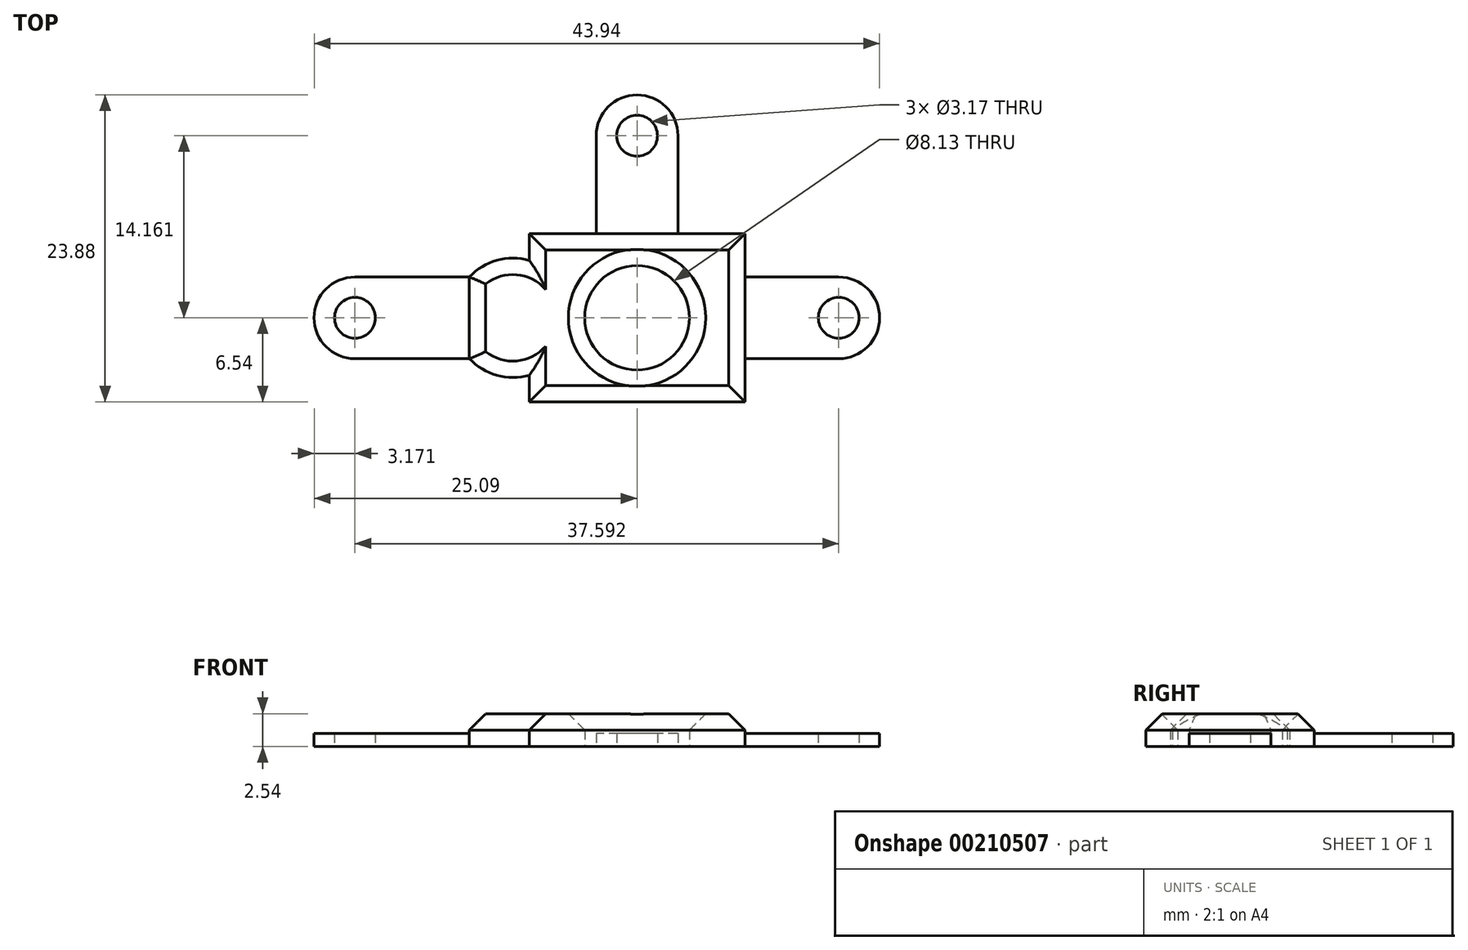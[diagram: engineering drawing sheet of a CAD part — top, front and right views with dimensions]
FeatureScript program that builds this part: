
annotation { "Feature Type Name" : "Feature", "Feature Type Description" : "" }
export const myFeature = defineFeature(function(context is Context, id is Id, definition is map)
    precondition{}
    {
        {
            var Q0;
            Q0=qCreatedBy(makeId("Top.planeOp"),FACE);
            var sketch = newSketch(context, id + "F0", { "sketchPlane" : qUnion([Q0])});
            skPoint(sketch, "E0.middle", {"position": v(0, 0) * mm});
            skArc(sketch, "E1", {"start": v(-8.38, 4.46) * mm, "mid": v(-10.89, 4.47) * mm, "end": v(-13.03, 3.17) * mm});
            skPoint(sketch, "E1.centerSnap0", {"position": v(-6.78, 0) * mm});
            skCircle(sketch, "E2", {"center": v(0, 0) * mm, "radius": 4.06 * mm});
            skArc(sketch, "E3", {"start": v(3.17, 14.16) * mm, "mid": v(0, 17.34) * mm, "end": v(-3.18, 14.16) * mm});
            skLineSegment(sketch, "E4", {"start": v(6.78, 0) * mm, "end": v(-13.03, 0) * mm, "construction": true});
            skLineSegment(sketch, "E5", {"start": v(3.17, 14.16) * mm, "end": v(3.18, 6.54) * mm});
            skLineSegment(sketch, "E6", {"start": v(-3.18, 14.16) * mm, "end": v(-3.18, 6.54) * mm});
            skArc(sketch, "E7.MirrorCS", {"start": v(3.17, -14.16) * mm, "mid": v(0, -17.34) * mm, "end": v(-3.18, -14.16) * mm});
            skLineSegment(sketch, "E8.MirrorCS", {"start": v(3.18, -14.16) * mm, "end": v(3.18, -6.54) * mm});
            skLineSegment(sketch, "E9.MirrorCS", {"start": v(-3.17, -14.16) * mm, "end": v(-3.17, -6.54) * mm});
            skArc(sketch, "E10", {"start": v(-21.92, 3.18) * mm, "mid": v(-25.1, 0) * mm, "end": v(-21.92, -3.18) * mm});
            skLineSegment(sketch, "E11", {"start": v(-21.92, 3.18) * mm, "end": v(-13.03, 3.18) * mm});
            skLineSegment(sketch, "E12", {"start": v(-21.92, -3.18) * mm, "end": v(-13.03, -3.18) * mm});
            skArc(sketch, "E13.trimOffspring", {"start": v(-13.03, -3.18) * mm, "mid": v(-10.89, -4.47) * mm, "end": v(-8.38, -4.46) * mm});
            skArc(sketch, "E14", {"start": v(15.67, -3.17) * mm, "mid": v(18.85, 0) * mm, "end": v(15.67, 3.18) * mm});
            skLineSegment(sketch, "E15", {"start": v(15.67, 3.18) * mm, "end": v(8.38, 3.17) * mm});
            skLineSegment(sketch, "E16", {"start": v(15.67, -3.17) * mm, "end": v(8.38, -3.17) * mm});
            skCircle(sketch, "E17", {"center": v(0, 14.16) * mm, "radius": 1.59 * mm});
            skCircle(sketch, "E18", {"center": v(15.67, 0) * mm, "radius": 1.59 * mm});
            skCircle(sketch, "E19", {"center": v(-21.92, 0) * mm, "radius": 1.59 * mm});
            skCircle(sketch, "E20", {"center": v(0, -14.16) * mm, "radius": 1.59 * mm});
            skLineSegment(sketch, "E21", {"start": v(-13.03, 3.18) * mm, "end": v(-13.03, -3.18) * mm});
            skLineSegment(sketch, "E22.bottom", {"start": v(8.38, 6.54) * mm, "end": v(-8.38, 6.54) * mm});
            skLineSegment(sketch, "E22.top", {"start": v(8.38, -6.54) * mm, "end": v(-8.38, -6.54) * mm});
            skLineSegment(sketch, "E22.left", {"start": v(8.38, 6.54) * mm, "end": v(8.38, -6.54) * mm});
            skLineSegment(sketch, "E22.right", {"start": v(-8.38, 6.54) * mm, "end": v(-8.38, -6.54) * mm});
            skSolve(sketch);
        }
        {
            var Q0;
            Q0=makeQuery(id+"F0.imprint","IMPRINT",FACE,{"disambiguationData":[TD([[makeQuery(id+"F0.imprint","IMPRINT",EDGE,{"derivedFrom":sQuery(id+"F0.wireOp",EDGE,"E0.bottom")}),1.0]])]});
            var Q1;
            Q1=makeQuery(id+"F0.imprint","IMPRINT",FACE,{"disambiguationData":[TD([[makeQuery(id+"F0.imprint","IMPRINT",EDGE,{"derivedFrom":sQuery(id+"F0.wireOp",EDGE,"E2")}),-1.0]])]});
            var Q2;
            {var subQ0=sQuery(id+"F0.wireOp",EDGE,"E1");Q2=makeQuery(id+"F0.imprint","IMPRINT",FACE,{"disambiguationData":[TD([[makeQuery(id+"F0.imprint","IMPRINT",EDGE,{"derivedFrom":subQ0}),1.0]])]});}
            extrude(context, id + "F1", {"entities" : qUnion([Q0, Q1, Q2]), "depth" : 2.54 * mm});
        }
        {
            var Q0;
            Q0=makeQuery(id+"F0.imprint","IMPRINT",FACE,{"disambiguationData":[TD([[makeQuery(id+"F0.imprint","IMPRINT",EDGE,{"derivedFrom":sQuery(id+"F0.wireOp",EDGE,"E10")}),1.0]])]});
            var Q1;
            Q1=makeQuery(id+"F0.imprint","IMPRINT",FACE,{"disambiguationData":[TD([[makeQuery(id+"F0.imprint","IMPRINT",EDGE,{"derivedFrom":sQuery(id+"F0.wireOp",EDGE,"E7.MirrorCS")}),-1.0]])]});
            var Q2;
            Q2=makeQuery(id+"F0.imprint","IMPRINT",FACE,{"disambiguationData":[TD([[makeQuery(id+"F0.imprint","IMPRINT",EDGE,{"derivedFrom":sQuery(id+"F0.wireOp",EDGE,"E3")}),1.0]])]});
            var Q3;
            Q3=makeQuery(id+"F0.imprint","IMPRINT",FACE,{"disambiguationData":[TD([[makeQuery(id+"F0.imprint","IMPRINT",EDGE,{"derivedFrom":sQuery(id+"F0.wireOp",EDGE,"E14")}),1.0]])]});
            extrude(context, id + "F2", {"entities" : qUnion([Q0, Q1, Q2, Q3]), "operationType" : NewBodyOperationType.ADD, "depth" : 1.02 * mm});
        }
        {
            var Q0;
            Q0=makeQuery(id+"F1.opExtrude","CAP_EDGE",EDGE,{"disambiguationData":[OSD([sQuery(id+"F0.wireOp",EDGE,"E22.top")])],"isStart":false});
            var Q1;
            Q1=makeQuery(id+"F1.opExtrude","CAP_EDGE",EDGE,{"disambiguationData":[OSD([sQuery(id+"F0.wireOp",EDGE,"E22.left")])],"isStart":false});
            var Q2;
            {var subQ0=sQuery(id+"F0.wireOp",EDGE,"E22.right");Q2=makeQuery(id+"F1.opExtrude","CAP_EDGE",EDGE,{"disambiguationData":[OSD([subQ0]),TDD([makeQuery(id+"F0.imprint","IMPRINT",EDGE,{"disambiguationData":[TD([[makeQuery(id+"F0.imprint","INTERSECT",VERTEX,{"derivedFrom":[sQuery(id+"F0.wireOp",EDGE,"E13.trimOffspring"),subQ0]}),-1.0]])],"derivedFrom":subQ0})])],"isStart":false});}
            var Q3;
            Q3=makeQuery(id+"F1.opExtrude","CAP_EDGE",EDGE,{"disambiguationData":[OSD([sQuery(id+"F0.wireOp",EDGE,"E13.trimOffspring")])],"isStart":false});
            var Q4;
            Q4=makeQuery(id+"F1.opExtrude","CAP_EDGE",EDGE,{"disambiguationData":[OSD([sQuery(id+"F0.wireOp",EDGE,"E21")])],"isStart":false});
            var Q5;
            Q5=makeQuery(id+"F1.opExtrude","CAP_EDGE",EDGE,{"disambiguationData":[OSD([sQuery(id+"F0.wireOp",EDGE,"E1")])],"isStart":false});
            var Q6;
            {var subQ0=sQuery(id+"F0.wireOp",EDGE,"E22.right");Q6=makeQuery(id+"F1.opExtrude","CAP_EDGE",EDGE,{"disambiguationData":[OSD([subQ0]),TDD([makeQuery(id+"F0.imprint","IMPRINT",EDGE,{"disambiguationData":[TD([[makeQuery(id+"F0.imprint","INTERSECT",VERTEX,{"derivedFrom":[sQuery(id+"F0.wireOp",EDGE,"E1"),subQ0]}),1.0]])],"derivedFrom":subQ0})])],"isStart":false});}
            var Q7;
            Q7=makeQuery(id+"F1.opExtrude","CAP_EDGE",EDGE,{"disambiguationData":[OSD([sQuery(id+"F0.wireOp",EDGE,"E22.bottom")])],"isStart":false});
            var Q8;
            Q8=makeQuery(id+"F1.opExtrude","CAP_EDGE",EDGE,{"disambiguationData":[OSD([sQuery(id+"F0.wireOp",EDGE,"E2")])],"isStart":false});
            chamfer(context, id + "F3", {"entities" : qUnion([Q0, Q1, Q2, Q3, Q4, Q5, Q6, Q7, Q8]), "chamferType" : ChamferType.OFFSET_ANGLE, "width" : 1.27 * mm, "oppositeDirection" : false, "angle" : 45 * degree, "tangentPropagation" : true});
        }
    });
